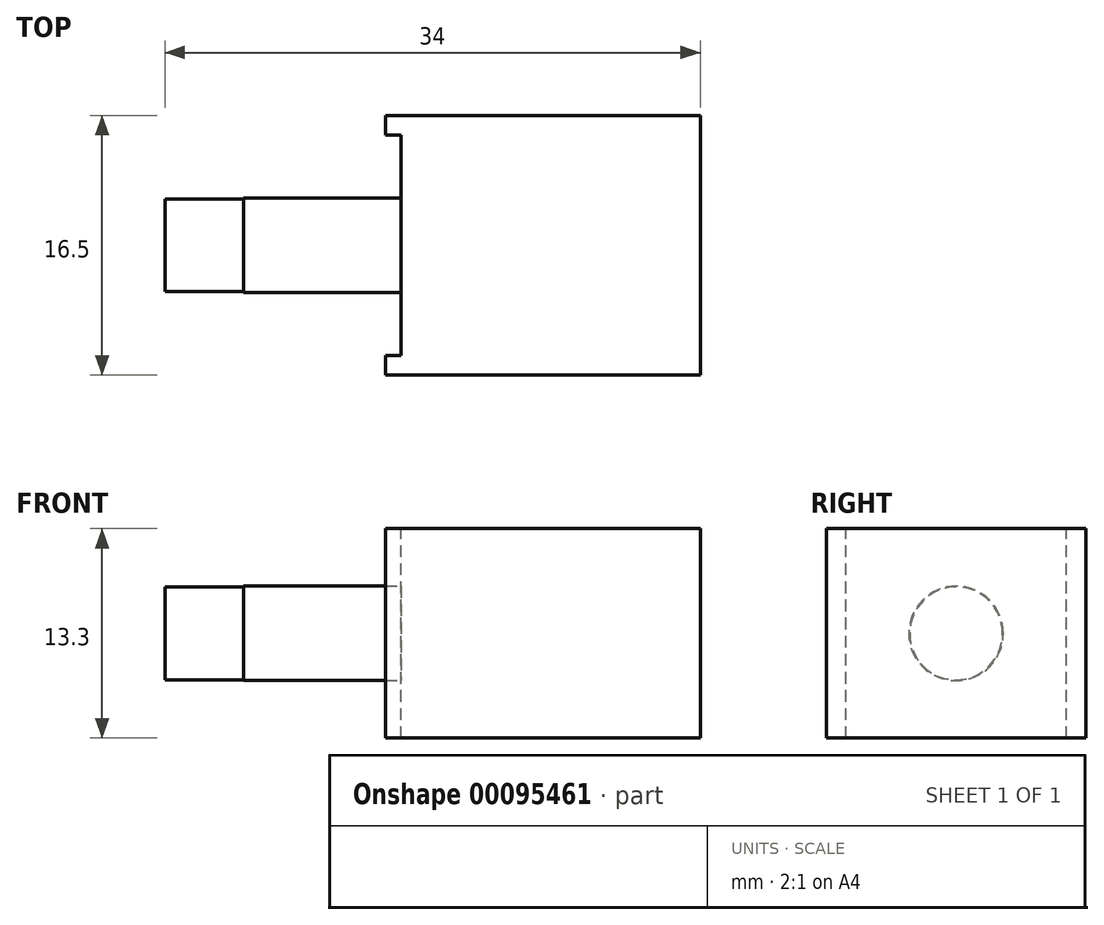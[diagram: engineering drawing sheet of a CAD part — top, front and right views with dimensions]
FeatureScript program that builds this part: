
annotation { "Feature Type Name" : "Feature", "Feature Type Description" : "" }
export const myFeature = defineFeature(function(context is Context, id is Id, definition is map)
    precondition{}
    {
        {
            var Q0;
            Q0=qCreatedBy(makeId("Top.planeOp"),FACE);
            var sketch = newSketch(context, id + "F0", { "sketchPlane" : qUnion([Q0])});
            skLineSegment(sketch, "E0.bottom", {"start": v(10, -8.25) * mm, "end": v(-10, -8.25) * mm});
            skLineSegment(sketch, "E0.top", {"start": v(10, 8.25) * mm, "end": v(-10, 8.25) * mm});
            skLineSegment(sketch, "E0.left", {"start": v(10, -8.25) * mm, "end": v(10, 8.25) * mm});
            skLineSegment(sketch, "E0.right", {"start": v(-10, -8.25) * mm, "end": v(-10, 8.25) * mm});
            skPoint(sketch, "E0.middle", {"position": v(0, 0) * mm});
            skSolve(sketch);
        }
        {
            var Q0;
            Q0 = qSketchRegion(id + "F0", true);
            extrude(context, id + "F1", {"entities" : qUnion([Q0]), "endBound" : BoundingType.SYMMETRIC, "depth" : 13.3 * mm});
        }
        {
            var Q0;
            Q0=makeQuery(id+"F1.opExtrude","SWEPT_FACE",FACE,{"disambiguationData":[OSD([sQuery(id+"F0.wireOp",EDGE,"E0.right")])]});
            var sketch = newSketch(context, id + "F2", { "sketchPlane" : qUnion([Q0])});
            skCircle(sketch, "E1", {"center": v(0, 0) * mm, "radius": 3 * mm});
            skSolve(sketch);
        }
        {
            var Q0;
            Q0=makeQuery(id+"F1.opExtrude","CAP_FACE",FACE,{"disambiguationData":[OSD([sQuery(id+"F0.wireOp",EDGE,"E0.bottom"),sQuery(id+"F0.wireOp",EDGE,"E0.top"),sQuery(id+"F0.wireOp",EDGE,"E0.left"),sQuery(id+"F0.wireOp",EDGE,"E0.right")])],"isStart":false});
            var sketch = newSketch(context, id + "F3", { "sketchPlane" : qUnion([Q0])});
            skLineSegment(sketch, "E2.bottom", {"start": v(-10, 7) * mm, "end": v(-9, 7) * mm});
            skLineSegment(sketch, "E2.top", {"start": v(-10, -7) * mm, "end": v(-9, -7) * mm});
            skLineSegment(sketch, "E2.left", {"start": v(-10, 7) * mm, "end": v(-10, -7) * mm});
            skLineSegment(sketch, "E2.right", {"start": v(-9, 7) * mm, "end": v(-9, -7) * mm});
            skLineSegment(sketch, "E3", {"start": v(-9, 0) * mm, "end": v(10, 0) * mm, "construction": true});
            skSolve(sketch);
        }
        {
            var Q0;
            Q0 = qSketchRegion(id + "F3", true);
            extrude(context, id + "F4", {"entities" : qUnion([Q0]), "operationType" : NewBodyOperationType.REMOVE, "endBound" : BoundingType.THROUGH_ALL, "oppositeDirection" : true, "depth" : 25 * mm});
        }
        {
            var Q0;
            Q0 = qSketchRegion(id + "F2", true);
            extrude(context, id + "F5", {"entities" : qUnion([Q0]), "operationType" : NewBodyOperationType.ADD, "depth" : 9 * mm, "hasSecondDirection" : true, "secondDirectionBound" : SecondDirectionBoundingType.UP_TO_NEXT, "secondDirectionOppositeDirection" : true, "secondDirectionDepth" : 25 * mm});
        }
        {
            var Q0;
            Q0=makeQuery(id+"F5.opExtrude","CAP_FACE",FACE,{"disambiguationData":[OSD([sQuery(id+"F2.wireOp",EDGE,"E1")])],"isStart":false});
            var sketch = newSketch(context, id + "F6", { "sketchPlane" : qUnion([Q0])});
            skCircle(sketch, "E4", {"center": v(0, 0) * mm, "radius": 2.95 * mm});
            skSolve(sketch);
        }
        {
            var Q0;
            Q0=makeQuery(id+"F6.imprint","IMPRINT",FACE,{"disambiguationData":[TD([[makeQuery(id+"F6.imprint","IMPRINT",EDGE,{"derivedFrom":sQuery(id+"F6.wireOp",EDGE,"E4")}),1.0]])]});
            extrude(context, id + "F7", {"entities" : qUnion([Q0]), "operationType" : NewBodyOperationType.ADD, "depth" : 5 * mm});
        }
    });
